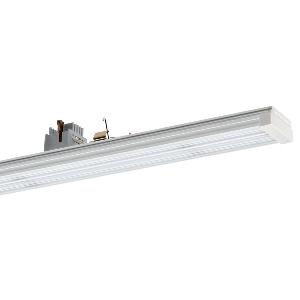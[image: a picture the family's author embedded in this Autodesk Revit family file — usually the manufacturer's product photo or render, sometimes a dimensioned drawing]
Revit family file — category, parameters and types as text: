
# Revit family: conveo_-_cvg_15000_850_w-p_ea_5_226848129-00804948_7561
name_source: partatom
category: Lighting Fixtures
units: mm (PartAtom-declared; Revit-internal decimal feet)

## family parameters
Cut with Voids When Loaded = No
Host = Face
Light Source = No
Part Type = Normal
Room Calculation Point = No
Round Connector Dimension = Use Diameter
Shared = No

## types (1)
- CONVEO - CVG 15000/850/W-P/EA/5 (1 x LED, 15100 lm, 5000K)
    Apparent Load = 100 VA
    Approval mark = CE
    CIE Flux Codes = 54 85 97 100 100
    Color Rendering = 80-89
    Color Temperature = 5000K
    Control Gear = Electronic ballast
    Default Elevation = 1800 mm
    Description = CVG 15000/850/W-P/EA/5|Continuous-row system|light source: LED|work equipment: Electronic ballast|connected load: 220-240 V, 50-60 Hz|Power consumption: approx. 100 W|luminous flux: 15100 lm|luminous efficacy: 151 lm/W|colour temperature: Cold white, ca. 5000 K|color rendering index (CRI): >= 80|chromaticity tolerance:  3 SDCM|System of protection: IP 54|class of protection: I|technology: Switchable|luminaire body|material: Aluminium|surface: Powder coatet|colour: White|lamp cover: Acrylic (PMMA), Satine|weight (net): approx. 2.2 kg|Fastening: Available separately|minimum ambient temperature: -25 ░C|maximum ambient temperature: 37 ░C|glare control: Prism optics (linear)|Approval mark: VDE - ENEC|
    Frequency = 50 Hz
    Height = 70 mm
    Lamp = 1 x LED
    Lamp Light Flux = 15100 lm
    Lamp count = 1
    Length = 1500 mm
    Luminous efficacy = 151 lm/W
    Manufacturer = Waldmann
    ModVariant = No
    Model = 226848129-00804948
    Mounting Place = Ceiling
    Mounting Type = Pendant
    Number of Poles = 1
    OnlyDefault = Yes
    Power Factor = 1
    Product Name = CONVEO - CVG 15000/850/W-P/EA/5
    Product group = Continuous-row system (industry)
    ProductGroupID = 301
    Protection Class = Protection class I
    Protection Degree = IP 54
    RLX_Detail_Level = 1
    RlxData = <blob elided: 132541 chars, md5=83365d92>
    Socket = socket
    Standby Power = 0 W
    System Light Flux = 15100 lm
    System Power = 100 W
    Type Comments = Product without accessories
    Type Image = 226848119-00804947-2p5.jpg
    URL = http://relux.com
    VarID = ---
    Voltage = 230 V
    Voltage Range = 220-240 V
    Weight = 0.00 kg
    Width = 64 mm

## geometry (parser evidence)
native form markers: Blend x4, Sweep x9
no freeform markers — native parametric forms only
